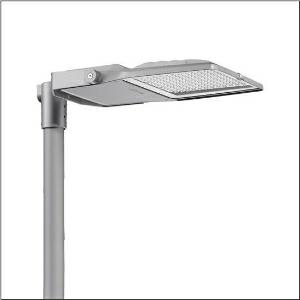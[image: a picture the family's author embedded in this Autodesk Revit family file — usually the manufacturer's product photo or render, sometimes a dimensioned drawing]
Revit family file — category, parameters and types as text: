
# Revit family: floodlight_fl_21_iq_midi___pl43_5xa7782e2a3a_72be
name_source: partatom
category: Lighting Fixtures
units: mm (PartAtom-declared; Revit-internal decimal feet)

## family parameters
Cut with Voids When Loaded = No
Host = Face
Light Source = No
Part Type = Normal
Room Calculation Point = No
Round Connector Dimension = Use Diameter
Shared = No

## types (1)
- --- (1 x LED, 27540 lm, 208.1 W, 3000K)
    Apparent Load = 208 VA
    CIE Flux Codes = 27 78 99 100 100
    Color Rendering = 70
    Color Temperature = 3000K
    Default Elevation = 1800 mm
    Description = Floodlight FL 21 iQ midi, floodlight, primary light control with lens, of PMMA, primary optical cover: protective disc, of toughened safety glass, transparent, light distribution: PL43, light emission: direct distribution, installation type: surface-mounted, LED, High Power LED, rated luminous flux: 27.540lm, luminous efficacy: 132lm/W, light colour: 730, colour temperature: 3000K, control gear: iQ Street-Remote/DALI, control: optimised constant luminous flux control (CLO 2.0), Desk-Remote (wireless, voltage-free reading and setting of iQ features in the workshop via application-optimized NFC function/RFID function), Smart-Wire, Night-Set, Temp-Guard, Auto-Match, Street-Remote, with terminal, 6-pole, mains connection: 220..240V, AC, 50/60Hz, start of lifetime: 208W, end of service life: 227W, reduction: 90W, luminaire housing, of diecast aluminium, powder-coated, Siteco® metallic grey (DB 702S), corrosivity category C5 mid according to DIN EN ISO 12944, suitable for swimming pools, chlorine-resistant, sealing non-destructively replaceable, please order mast flange separately, mast bracket, of steel, galvanised, powder-coated, Siteco® metallic grey (DB 702S), protection rating (complete): IP66, insulation class (complete): insulation class II (safety insulation), certification: CE, ENEC, VDE, protection symbol: D, impact resistance: IK08, permissible operating ambient temperature: -40..+40°C, permissible operating ambient temperature for outdoor applications: -40..+50°C, standard: DIN EN 12944, LABS conformity tested according to VDMA 24364:2018-05, packaging unit: 1 piece

Light Distribution: PL43
    Height = 76 mm
    Lamp = 1 x LED
    Lamp Light Flux = 27540 lm
    Lamp Power = 208.1 W
    Lamp count = 1
    Length = 657 mm
    Luminous efficacy = 132 lm/W
    Manufacturer = Siteco
    ModVariant = No
    Model = 5XA7782E2A3A
    Number of Poles = 1
    OnlyDefault = Yes
    Power Factor = 1
    Product Name = Floodlight FL 21 iQ midi | PL43
    Product group = floodlight | pylon annexe
    ProductGroupID = 6201
    Protection Class = Protection class II
    Protection Degree = IP 66
    RLX_Detail_Level = 1
    RLX_Emergency_Light_Flux = 0 lm
    RLX_Emergency_Type = 0
    RLX_Emergency_Type_DB = No
    RlxData = <blob elided: 153665 chars, md5=e0451395>
    Socket = socket
    Standby Power = 0 W
    System Light Flux = 27540 lm
    System Power = 208 W
    Type Comments = factory setting: luminous flux: 100 % | dim-lin: 254 | 710 mA
    Type Image = l_1007123.jpg
    URL = http://relux.com
    VarID = @adj_126619
    Voltage = 0 V
    Weight = 0.00 kg
    Width = 442 mm

## geometry (parser evidence)
native form markers: Blend x4, Sweep x11
no freeform markers — native parametric forms only
